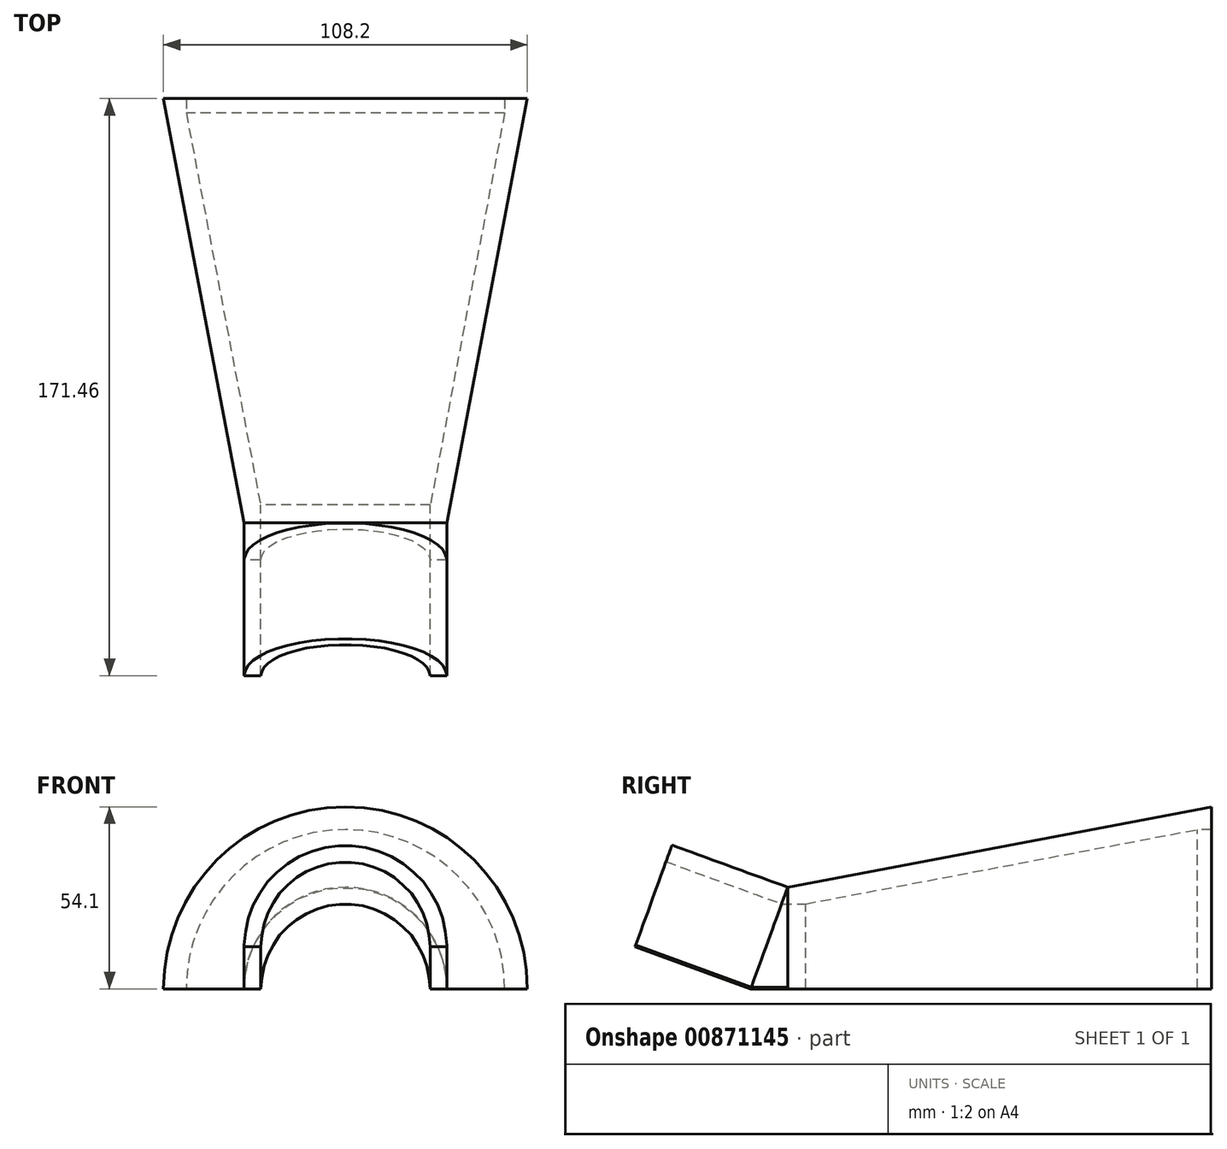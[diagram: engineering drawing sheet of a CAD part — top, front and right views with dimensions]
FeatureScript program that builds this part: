
annotation { "Feature Type Name" : "Feature", "Feature Type Description" : "" }
export const myFeature = defineFeature(function(context is Context, id is Id, definition is map)
    precondition{}
    {
        {
            var Q0;
            Q0=qCreatedBy(makeId("Top.planeOp"),FACE);
            var sketch = newSketch(context, id + "F0", { "sketchPlane" : qUnion([Q0])});
            skLineSegment(sketch, "E0", {"start": v(0, 0) * mm, "end": v(0, 57.46) * mm});
            skLineSegment(sketch, "E1", {"start": v(0, 57.46) * mm, "end": v(-54.1, 57.46) * mm});
            skLineSegment(sketch, "E2", {"start": v(-54.1, 57.46) * mm, "end": v(-30.2, -68.58) * mm});
            skLineSegment(sketch, "E3", {"start": v(-30.2, -68.58) * mm, "end": v(0, -68.58) * mm});
            skLineSegment(sketch, "E4", {"start": v(0, -68.58) * mm, "end": v(0, 0) * mm});
            skLineSegment(sketch, "E5", {"start": v(0, 53.17) * mm, "end": v(-47.34, 53.17) * mm});
            skLineSegment(sketch, "E6", {"start": v(-47.34, 53.17) * mm, "end": v(-25.26, -63.27) * mm});
            skLineSegment(sketch, "E7", {"start": v(-25.26, -63.27) * mm, "end": v(0, -63.27) * mm});
            skLineSegment(sketch, "E8", {"start": v(-6.3, 53.17) * mm, "end": v(-6.3, -63.27) * mm});
            skLineSegment(sketch, "E9", {"start": v(-6.3, -63.27) * mm, "end": v(-6.3, -68.58) * mm});
            skLineSegment(sketch, "E10", {"start": v(-6.3, 53.17) * mm, "end": v(-6.3, 57.46) * mm});
            skSolve(sketch);
        }
        {
            var Q0;
            {var subQ5=sQuery(id+"F0.wireOp",EDGE,"E2");Q0=makeQuery(id+"F0.imprint","IMPRINT",FACE,{"disambiguationData":[TD([[makeQuery(id+"F0.imprint","IMPRINT",EDGE,{"derivedFrom":subQ5}),1.0]])]});}
            var Q1;
            Q1=sQuery(id+"F0.wireOp",EDGE,"E4");
            revolve(context, id + "F1", {"surfaceOperationType" : NewSurfaceOperationType.NEW, "entities" : qUnion([Q0]), "axis" : qUnion([Q1]), "revolveType" : RevolveType.ONE_DIRECTION, "angle" : 180 * degree});
        }
        {
            var Q0;
            Q0=makeQuery(id+"F1.opRevolve","SWEPT_FACE",FACE,{"disambiguationData":[OSD([sQuery(id+"F0.wireOp",EDGE,"E5")])]});
            extrude(context, id + "F2", {"entities" : qUnion([Q0]), "operationType" : NewBodyOperationType.REMOVE, "oppositeDirection" : true, "depth" : 25.4 * mm, "offsetDistance" : 25.4 * mm});
        }
        {
            var Q0;
            Q0=makeQuery(id+"F1.opRevolve","SWEPT_FACE",FACE,{"disambiguationData":[OSD([sQuery(id+"F0.wireOp",EDGE,"E7")])]});
            extrude(context, id + "F3", {"entities" : qUnion([Q0]), "operationType" : NewBodyOperationType.REMOVE, "oppositeDirection" : true, "depth" : 25.4 * mm, "offsetDistance" : 25.4 * mm});
        }
        {
            var Q0;
            Q0=qCreatedBy(makeId("Right.planeOp"),FACE);
            var sketch = newSketch(context, id + "F4", { "sketchPlane" : qUnion([Q0])});
            skLineSegment(sketch, "E11", {"start": v(-68.58, 0) * mm, "end": v(-68.58, 30.34) * mm});
            skLineSegment(sketch, "E12", {"start": v(-68.58, 30.34) * mm, "end": v(-79.63, 0) * mm});
            skLineSegment(sketch, "E13", {"start": v(-79.63, 0) * mm, "end": v(-68.58, 0) * mm});
            skLineSegment(sketch, "E14", {"start": v(-68.58, 25.26) * mm, "end": v(-70.43, 25.26) * mm});
            skSolve(sketch);
        }
        {
            var Q0;
            {var subQ0=sQuery(id+"F4.wireOp",EDGE,"E13");Q0=makeQuery(id+"F4.imprint","IMPRINT",FACE,{"disambiguationData":[TD([[makeQuery(id+"F4.imprint","IMPRINT",EDGE,{"derivedFrom":subQ0}),1.0]])]});}
            var Q1;
            {var subQ3=sQuery(id+"F4.wireOp",EDGE,"E14");Q1=makeQuery(id+"F4.imprint","IMPRINT",FACE,{"disambiguationData":[TD([[makeQuery(id+"F4.imprint","IMPRINT",EDGE,{"derivedFrom":subQ3}),-1.0]])]});}
            extrude(context, id + "F5", {"entities" : qUnion([Q0, Q1]), "operationType" : NewBodyOperationType.ADD, "depth" : 30.2 * mm, "offsetDistance" : 25.4 * mm});
        }
        {
            var Q0;
            Q0=makeQuery(id+"F5.opExtrude","CAP_FACE",FACE,{"disambiguationData":[OSD([sQuery(id+"F4.wireOp",EDGE,"E11"),sQuery(id+"F4.wireOp",EDGE,"E12"),sQuery(id+"F4.wireOp",EDGE,"E13"),sQuery(id+"F4.wireOp",EDGE,"E14")])],"isStart":true});
            var Q1;
            {var subQ3=sQuery(id+"F4.wireOp",EDGE,"E14");Q1=makeQuery(id+"F4.imprint","IMPRINT",FACE,{"disambiguationData":[TD([[makeQuery(id+"F4.imprint","IMPRINT",EDGE,{"derivedFrom":subQ3}),-1.0]])]});}
            extrude(context, id + "F6", {"entities" : qUnion([Q0, Q1]), "operationType" : NewBodyOperationType.ADD, "depth" : 30.2 * mm, "offsetDistance" : 25.4 * mm});
        }
        {
            var Q0;
            {var subQ0=sQuery(id+"F0.wireOp",EDGE,"E3");var subQ1=makeQuery(id+"F1.opRevolve","SWEPT_FACE",FACE,{"disambiguationData":[OSD([subQ0])]});var subQ2=sQuery(id+"F4.wireOp",EDGE,"E13");var subQ3=sQuery(id+"F4.wireOp",EDGE,"E12");var subQ4=sQuery(id+"F4.wireOp",EDGE,"E11");var subQ5=makeQuery(id+"F5.opExtrude","CAP_FACE",FACE,{"disambiguationData":[OSD([subQ4,subQ3,subQ2])],"isStart":true});var subQ6=makeQuery(id+"F5.opExtrude","CAP_EDGE",EDGE,{"disambiguationData":[OSD([subQ4])],"isStart":true});var subQ7=makeQuery(id+"F5.opExtrude","SWEPT_FACE",FACE,{"disambiguationData":[OSD([subQ4])]});var subQ8=sQuery(id+"F0.wireOp",EDGE,"E2");var subQ9=makeQuery(id+"F1.opRevolve","SWEPT_FACE",FACE,{"disambiguationData":[OSD([subQ8])]});Q0=makeQuery(id+"F6.boolean.opBoolean","MERGE",FACE,{"derivedFrom":[makeQuery(id+"F5.boolean.opBoolean","SPLIT",FACE,{"disambiguationData":[TD([subQ9])],"derivedFrom":subQ7}),makeQuery(id+"F6.opExtrude","SWEPT_FACE",FACE,{"disambiguationData":[OSD([subQ4]),TDD([makeQuery(id+"F4.imprint","IMPRINT",EDGE,{"disambiguationData":[TD([[makeQuery(id+"F4.imprint","INTERSECT",VERTEX,{"derivedFrom":[subQ4,subQ3]}),1.0]])],"derivedFrom":subQ4})])]}),makeQuery(id+"F6.opExtrude","SWEPT_FACE",FACE,{"disambiguationData":[OSD([subQ4]),TDD([makeQuery(id+"F5.boolean.opBoolean","SPLIT",EDGE,{"disambiguationData":[topologyDisambiguationEdgeConnected([subQ7,subQ5]),TD([makeQuery(id+"F5.opExtrude","SWEPT_FACE",FACE,{"disambiguationData":[OSD([subQ2])]})])],"derivedFrom":subQ6}),makeQuery(id+"F5.boolean.opBoolean","SPLIT",EDGE,{"disambiguationData":[topologyDisambiguationEdgeConnected([subQ7,subQ5]),TD([subQ9])],"derivedFrom":subQ6}),makeQuery(id+"F5.boolean.opBoolean","SPLIT",EDGE,{"disambiguationData":[topologyDisambiguationEdgeConnected([subQ1,subQ5])],"derivedFrom":subQ6})])]})]});}
            extrude(context, id + "F7", {"entities" : qUnion([Q0]), "operationType" : NewBodyOperationType.REMOVE, "oppositeDirection" : true, "depth" : 25.4 * mm, "offsetDistance" : 25.4 * mm});
        }
        {
            var Q0;
            {var subQ0=sQuery(id+"F0.wireOp",EDGE,"E3");var subQ1=makeQuery(id+"F1.opRevolve","SWEPT_FACE",FACE,{"disambiguationData":[OSD([subQ0])]});var subQ2=sQuery(id+"F4.wireOp",EDGE,"E13");var subQ3=sQuery(id+"F4.wireOp",EDGE,"E12");var subQ4=sQuery(id+"F4.wireOp",EDGE,"E11");var subQ5=makeQuery(id+"F5.opExtrude","CAP_FACE",FACE,{"disambiguationData":[OSD([subQ4,subQ3,subQ2])],"isStart":true});var subQ6=makeQuery(id+"F5.opExtrude","CAP_EDGE",EDGE,{"disambiguationData":[OSD([subQ4])],"isStart":true});var subQ7=makeQuery(id+"F5.opExtrude","SWEPT_FACE",FACE,{"disambiguationData":[OSD([subQ4])]});var subQ8=sQuery(id+"F0.wireOp",EDGE,"E2");var subQ13=makeQuery(id+"F5.opExtrude","SWEPT_FACE",FACE,{"disambiguationData":[OSD([subQ2])]});Q0=makeQuery(id+"F6.boolean.opBoolean","MERGE",FACE,{"derivedFrom":[makeQuery(id+"F5.boolean.opBoolean","SPLIT",FACE,{"disambiguationData":[TD([subQ13])],"derivedFrom":subQ7}),makeQuery(id+"F6.opExtrude","SWEPT_FACE",FACE,{"disambiguationData":[OSD([subQ4]),TDD([makeQuery(id+"F4.imprint","IMPRINT",EDGE,{"disambiguationData":[TD([[makeQuery(id+"F4.imprint","INTERSECT",VERTEX,{"derivedFrom":[subQ4,subQ3]}),1.0]])],"derivedFrom":subQ4})])]}),makeQuery(id+"F6.opExtrude","SWEPT_FACE",FACE,{"disambiguationData":[OSD([subQ4]),TDD([makeQuery(id+"F5.boolean.opBoolean","SPLIT",EDGE,{"disambiguationData":[topologyDisambiguationEdgeConnected([subQ7,subQ5]),TD([subQ13])],"derivedFrom":subQ6}),makeQuery(id+"F5.boolean.opBoolean","SPLIT",EDGE,{"disambiguationData":[topologyDisambiguationEdgeConnected([subQ7,subQ5]),TD([makeQuery(id+"F1.opRevolve","SWEPT_FACE",FACE,{"disambiguationData":[OSD([subQ8])]})])],"derivedFrom":subQ6}),makeQuery(id+"F5.boolean.opBoolean","SPLIT",EDGE,{"disambiguationData":[topologyDisambiguationEdgeConnected([subQ1,subQ5])],"derivedFrom":subQ6})])]})]});}
            extrude(context, id + "F8", {"entities" : qUnion([Q0]), "operationType" : NewBodyOperationType.REMOVE, "oppositeDirection" : true, "depth" : 25.4 * mm, "offsetDistance" : 25.4 * mm});
        }
        {
            var Q0;
            {var subQ0=sQuery(id+"F4.wireOp",EDGE,"E12");Q0=makeQuery(id+"F6.boolean.opBoolean","MERGE",FACE,{"derivedFrom":[makeQuery(id+"F5.opExtrude","SWEPT_FACE",FACE,{"disambiguationData":[OSD([subQ0])]}),makeQuery(id+"F6.opExtrude","SWEPT_FACE",FACE,{"disambiguationData":[OSD([subQ0]),TDD([makeQuery(id+"F4.imprint","IMPRINT",EDGE,{"disambiguationData":[TD([[makeQuery(id+"F4.imprint","INTERSECT",VERTEX,{"derivedFrom":[sQuery(id+"F4.wireOp",EDGE,"E11"),subQ0]}),-1.0]])],"derivedFrom":subQ0})])]}),makeQuery(id+"F6.opExtrude","SWEPT_FACE",FACE,{"disambiguationData":[OSD([subQ0]),TDD([makeQuery(id+"F5.opExtrude","CAP_EDGE",EDGE,{"disambiguationData":[OSD([subQ0])],"isStart":true})])]})]});}
            extrude(context, id + "F9", {"entities" : qUnion([Q0]), "operationType" : NewBodyOperationType.ADD, "depth" : 36.58 * mm, "offsetDistance" : 25.4 * mm});
        }
    });
